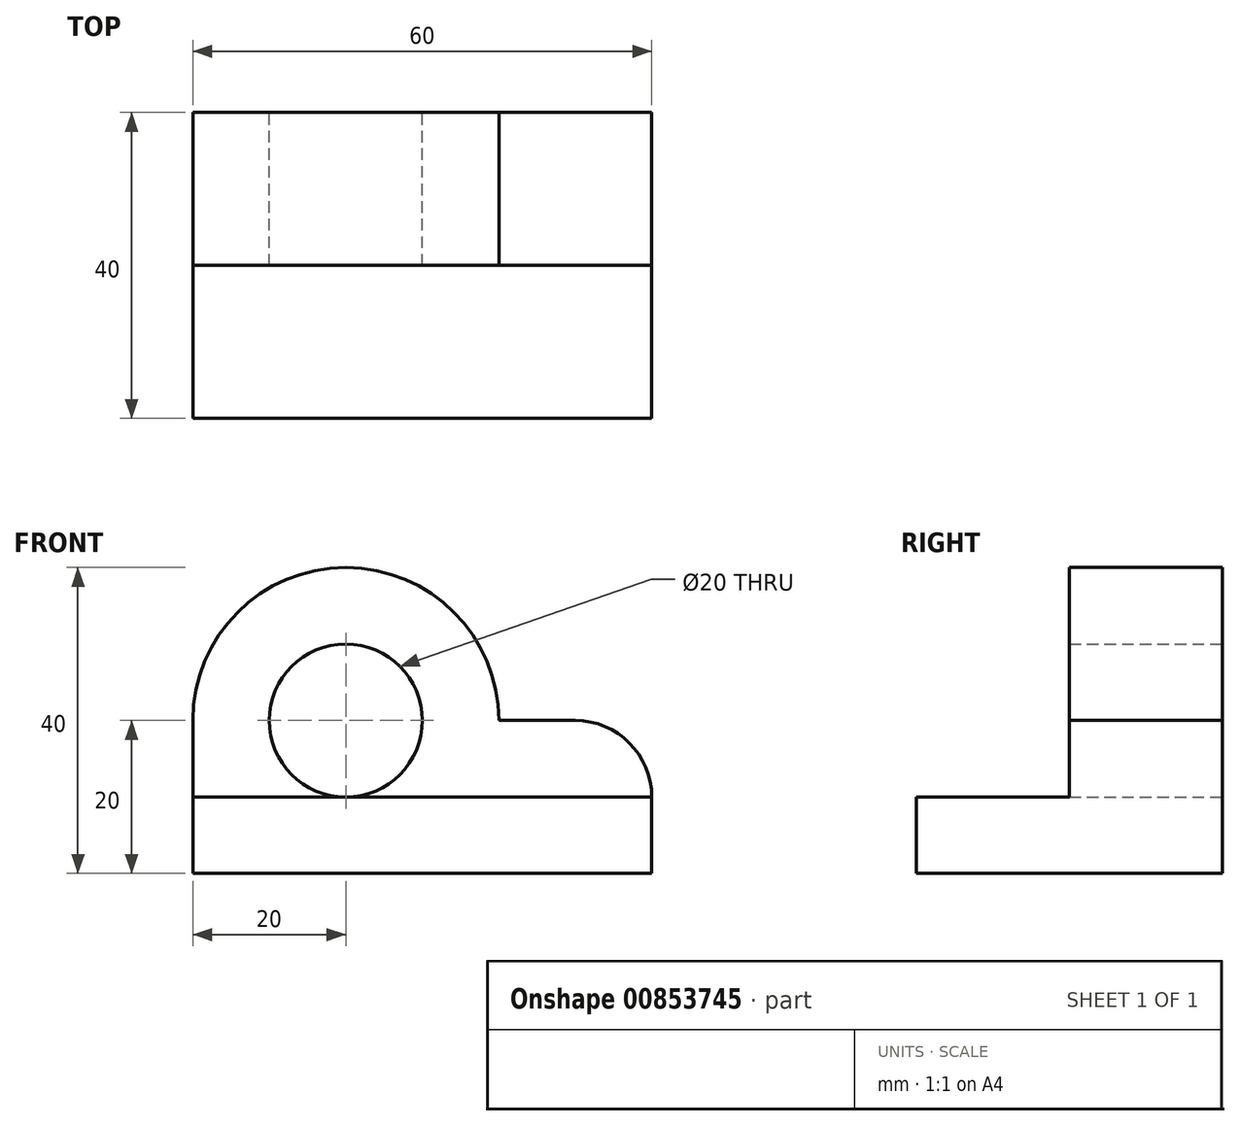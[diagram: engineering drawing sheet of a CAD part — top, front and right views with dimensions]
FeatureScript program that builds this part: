
annotation { "Feature Type Name" : "Feature", "Feature Type Description" : "" }
export const myFeature = defineFeature(function(context is Context, id is Id, definition is map)
    precondition{}
    {
        {
            var Q0;
            Q0=qCreatedBy(makeId("Front.planeOp"),FACE);
            var sketch = newSketch(context, id + "F0", { "sketchPlane" : qUnion([Q0])});
            skLineSegment(sketch, "E0.bottom", {"start": v(0, 0) * mm, "end": v(60, 0) * mm});
            skLineSegment(sketch, "E0.top", {"start": v(0, 10) * mm, "end": v(60, 10) * mm});
            skLineSegment(sketch, "E0.left", {"start": v(0, 0) * mm, "end": v(0, 10) * mm});
            skLineSegment(sketch, "E0.right", {"start": v(60, 0) * mm, "end": v(60, 10) * mm});
            skLineSegment(sketch, "E1.top", {"start": v(0, 20) * mm, "end": v(10, 20) * mm});
            skLineSegment(sketch, "E1.left", {"start": v(0, 10) * mm, "end": v(0, 20) * mm});
            skLineSegment(sketch, "E1.right", {"start": v(60, 10) * mm, "end": v(60, 10) * mm});
            skPoint(sketch, "E2.visualSharp", {"position": v(60, 20) * mm});
            skArc(sketch, "E2.filletArc", {"start": v(60, 10) * mm, "mid": v(57.07, 17.07) * mm, "end": v(50, 20) * mm});
            skCircle(sketch, "E3", {"center": v(20, 20) * mm, "radius": 10 * mm});
            skArc(sketch, "E4", {"start": v(40, 20) * mm, "mid": v(20, 40) * mm, "end": v(0, 20) * mm});
            skLineSegment(sketch, "E5.trimOffspring", {"start": v(30, 20) * mm, "end": v(50, 20) * mm});
            skSolve(sketch);
        }
        {
            var Q0;
            Q0=makeQuery(id+"F0.imprint","IMPRINT",FACE,{"disambiguationData":[TD([[makeQuery(id+"F0.imprint","IMPRINT",EDGE,{"derivedFrom":sQuery(id+"F0.wireOp",EDGE,"E0.bottom")}),1.0]])]});
            var Q1;
            {var subQ4=sQuery(id+"F0.wireOp",EDGE,"E2.filletArc");Q1=makeQuery(id+"F0.imprint","IMPRINT",FACE,{"disambiguationData":[TD([[makeQuery(id+"F0.imprint","IMPRINT",EDGE,{"derivedFrom":subQ4}),1.0]])]});}
            var Q2;
            {var subQ0=sQuery(id+"F0.wireOp",EDGE,"E1.left");Q2=makeQuery(id+"F0.imprint","IMPRINT",FACE,{"disambiguationData":[TD([[makeQuery(id+"F0.imprint","IMPRINT",EDGE,{"derivedFrom":subQ0}),-1.0]])]});}
            var Q3;
            {var subQ4=sQuery(id+"F0.wireOp",EDGE,"E4");Q3=makeQuery(id+"F0.imprint","IMPRINT",FACE,{"disambiguationData":[TD([[makeQuery(id+"F0.imprint","IMPRINT",EDGE,{"derivedFrom":subQ4}),1.0]])]});}
            extrude(context, id + "F1", {"entities" : qUnion([Q0, Q1, Q2, Q3]), "depth" : 20 * mm, "offsetDistance" : 25 * mm});
        }
        {
            var Q0;
            Q0=makeQuery(id+"F1.opExtrude","CAP_FACE",FACE,{"disambiguationData":[OSD([sQuery(id+"F0.wireOp",EDGE,"E0.bottom"),sQuery(id+"F0.wireOp",EDGE,"E0.left"),sQuery(id+"F0.wireOp",EDGE,"E0.right"),sQuery(id+"F0.wireOp",EDGE,"E1.left"),sQuery(id+"F0.wireOp",EDGE,"E2.filletArc"),sQuery(id+"F0.wireOp",EDGE,"E3"),sQuery(id+"F0.wireOp",EDGE,"E4"),sQuery(id+"F0.wireOp",EDGE,"E5.trimOffspring")])],"isStart":false});
            var sketch = newSketch(context, id + "F2", { "sketchPlane" : qUnion([Q0])});
            skLineSegment(sketch, "E6.bottom", {"start": v(0, 0) * mm, "end": v(60, 0) * mm});
            skLineSegment(sketch, "E6.top", {"start": v(0, 10) * mm, "end": v(60, 10) * mm});
            skLineSegment(sketch, "E6.left", {"start": v(0, 0) * mm, "end": v(0, 10) * mm});
            skLineSegment(sketch, "E6.right", {"start": v(60, 0) * mm, "end": v(60, 10) * mm});
            skSolve(sketch);
        }
        {
            var Q0;
            Q0=makeQuery(id+"F2.imprint","IMPRINT",FACE,{"disambiguationData":[TD([[makeQuery(id+"F2.imprint","IMPRINT",EDGE,{"derivedFrom":sQuery(id+"F2.wireOp",EDGE,"E6.bottom")}),1.0]])]});
            extrude(context, id + "F3", {"entities" : qUnion([Q0]), "operationType" : NewBodyOperationType.ADD, "depth" : 20 * mm, "offsetDistance" : 25 * mm});
        }
    });
